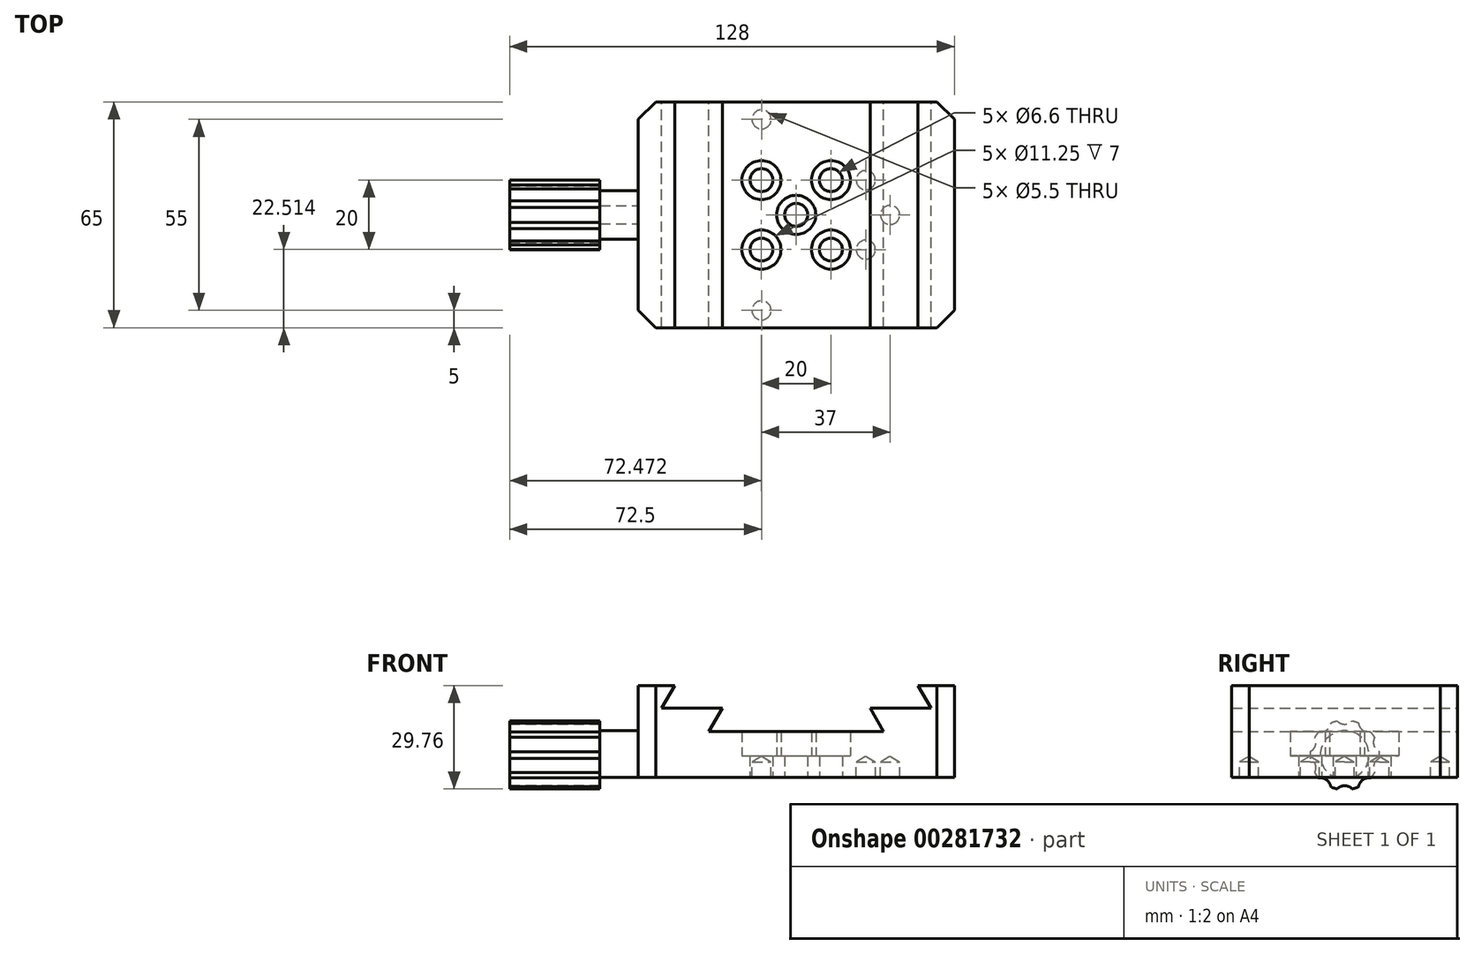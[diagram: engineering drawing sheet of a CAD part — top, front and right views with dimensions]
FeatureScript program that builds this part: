
annotation { "Feature Type Name" : "Feature", "Feature Type Description" : "" }
export const myFeature = defineFeature(function(context is Context, id is Id, definition is map)
    precondition{}
    {
        {
            var Q0;
            Q0=qCreatedBy(makeId("Front.planeOp"),FACE);
            var sketch = newSketch(context, id + "F0", { "sketchPlane" : qUnion([Q0])});
            skLineSegment(sketch, "E0.bottom", {"start": v(45.5, 13.25) * mm, "end": v(35, 13.25) * mm});
            skLineSegment(sketch, "E0.top", {"start": v(45.5, -13.25) * mm, "end": v(-45.5, -13.25) * mm});
            skLineSegment(sketch, "E0.left", {"start": v(45.5, 13.25) * mm, "end": v(45.5, -13.25) * mm});
            skLineSegment(sketch, "E0.right", {"start": v(-45.5, 13.25) * mm, "end": v(-45.5, -13.25) * mm});
            skPoint(sketch, "E0.middle", {"position": v(0, 0) * mm});
            skLineSegment(sketch, "E1", {"start": v(-35, 13.25) * mm, "end": v(-38.75, 6.75) * mm});
            skLineSegment(sketch, "E2", {"start": v(-38.75, 6.75) * mm, "end": v(-21.25, 6.75) * mm});
            skLineSegment(sketch, "E3", {"start": v(-25.15, 0) * mm, "end": v(0, 0) * mm});
            skLineSegment(sketch, "E4", {"start": v(-25.15, 0) * mm, "end": v(-21.25, 6.75) * mm});
            skLineSegment(sketch, "E5.MirrorCS", {"start": v(25.15, 0) * mm, "end": v(0, 0) * mm});
            skLineSegment(sketch, "E6.MirrorCS", {"start": v(25.15, 0) * mm, "end": v(21.25, 6.75) * mm});
            skLineSegment(sketch, "E7.MirrorCS", {"start": v(35, 13.25) * mm, "end": v(38.75, 6.75) * mm});
            skLineSegment(sketch, "E8.MirrorCS", {"start": v(38.75, 6.75) * mm, "end": v(21.25, 6.75) * mm});
            skLineSegment(sketch, "E9.trimOffspring", {"start": v(-35, 13.25) * mm, "end": v(-45.5, 13.25) * mm});
            skSolve(sketch);
        }
        {
            var Q0;
            Q0 = qSketchRegion(id + "F0", true);
            extrude(context, id + "F1", {"entities" : qUnion([Q0]), "depth" : 65 * mm, "offsetDistance" : 25 * mm});
        }
        {
            var Q0;
            Q0=makeQuery(id+"F1.opExtrude","CAP_EDGE",EDGE,{"disambiguationData":[OSD([sQuery(id+"F0.wireOp",EDGE,"E0.left")])],"isStart":false});
            var Q1;
            Q1=makeQuery(id+"F1.opExtrude","CAP_EDGE",EDGE,{"disambiguationData":[OSD([sQuery(id+"F0.wireOp",EDGE,"E0.left")])],"isStart":true});
            var Q2;
            Q2=makeQuery(id+"F1.opExtrude","CAP_EDGE",EDGE,{"disambiguationData":[OSD([sQuery(id+"F0.wireOp",EDGE,"E0.right")])],"isStart":false});
            var Q3;
            Q3=makeQuery(id+"F1.opExtrude","CAP_EDGE",EDGE,{"disambiguationData":[OSD([sQuery(id+"F0.wireOp",EDGE,"E0.right")])],"isStart":true});
            chamfer(context, id + "F2", {"entities" : qUnion([Q0, Q1, Q2, Q3]), "width" : 5 * mm, "tangentPropagation" : true});
        }
        {
            var Q0;
            Q0=makeQuery(id+"F1.opExtrude","SWEPT_FACE",FACE,{"disambiguationData":[OSD([sQuery(id+"F0.wireOp",EDGE,"E0.top")])]});
            var sketch = newSketch(context, id + "F3", { "sketchPlane" : qUnion([Q0])});
            skLineSegment(sketch, "E10", {"start": v(-58.08, 32.5) * mm, "end": v(66.9, 32.5) * mm, "construction": true});
            skLineSegment(sketch, "E11", {"start": v(0, 65) * mm, "end": v(0, 32.5) * mm, "construction": true});
            skLineSegment(sketch, "E12", {"start": v(0, 32.5) * mm, "end": v(0, 0) * mm, "construction": true});
            skLineSegment(sketch, "E13", {"start": v(-52.73, 42.5) * mm, "end": v(64.58, 42.5) * mm, "construction": true});
            skLineSegment(sketch, "E14", {"start": v(-52.06, 22.5) * mm, "end": v(64.58, 22.5) * mm, "construction": true});
            skLineSegment(sketch, "E15", {"start": v(10, 71.2) * mm, "end": v(10, -10.8) * mm, "construction": true});
            skLineSegment(sketch, "E16", {"start": v(-10, 70.97) * mm, "end": v(-10, -12.66) * mm, "construction": true});
            skCircle(sketch, "E17", {"center": v(-10, 42.5) * mm, "radius": 3.25 * mm});
            skCircle(sketch, "E18", {"center": v(10, 42.5) * mm, "radius": 3.25 * mm});
            skCircle(sketch, "E19", {"center": v(10, 22.5) * mm, "radius": 3.25 * mm});
            skCircle(sketch, "E20", {"center": v(-10, 22.5) * mm, "radius": 3.25 * mm});
            skCircle(sketch, "E21", {"center": v(0, 32.5) * mm, "radius": 3.25 * mm});
            skLineSegment(sketch, "E22", {"start": v(20, -6.44) * mm, "end": v(20, 70.45) * mm, "construction": true});
            skLineSegment(sketch, "E23", {"start": v(27, -7.6) * mm, "end": v(27, 72.31) * mm, "construction": true});
            skCircle(sketch, "E24", {"center": v(27, 32.5) * mm, "radius": 4.57 * mm});
            skCircle(sketch, "E25", {"center": v(20, 22.5) * mm, "radius": 3.73 * mm});
            skCircle(sketch, "E26", {"center": v(20, 42.5) * mm, "radius": 4.4 * mm});
            skLineSegment(sketch, "E27", {"start": v(35.3, 5) * mm, "end": v(-26.02, 5) * mm, "construction": true});
            skLineSegment(sketch, "E28", {"start": v(33.92, 60) * mm, "end": v(-26.02, 60) * mm, "construction": true});
            skCircle(sketch, "E29", {"center": v(-10, 5) * mm, "radius": 6.46 * mm});
            skCircle(sketch, "E30", {"center": v(-10, 60) * mm, "radius": 6.14 * mm});
            skSolve(sketch);
        }
        {
            var Q0;
            Q0=makeQuery(id+"F1.opExtrude","SWEPT_FACE",FACE,{"disambiguationData":[OSD([sQuery(id+"F0.wireOp",EDGE,"E3"),sQuery(id+"F0.wireOp",EDGE,"E5.MirrorCS")])]});
            var sketch = newSketch(context, id + "F4", { "sketchPlane" : qUnion([Q0])});
            skLineSegment(sketch, "E31", {"start": v(-58.1, -32.49) * mm, "end": v(66.88, -32.49) * mm, "construction": true});
            skLineSegment(sketch, "E32", {"start": v(-0.03, 0.01) * mm, "end": v(-0.03, -32.49) * mm, "construction": true});
            skLineSegment(sketch, "E33", {"start": v(-0.03, -32.49) * mm, "end": v(-0.03, -64.99) * mm, "construction": true});
            skLineSegment(sketch, "E34", {"start": v(-52.76, -22.49) * mm, "end": v(64.55, -22.49) * mm, "construction": true});
            skLineSegment(sketch, "E35", {"start": v(-52.1, -42.49) * mm, "end": v(64.55, -42.49) * mm, "construction": true});
            skLineSegment(sketch, "E36", {"start": v(9.97, 6.21) * mm, "end": v(9.97, -75.79) * mm, "construction": true});
            skLineSegment(sketch, "E37", {"start": v(-10.03, 5.98) * mm, "end": v(-10.03, -77.65) * mm, "construction": true});
            skCircle(sketch, "E38", {"center": v(-10.03, -22.49) * mm, "radius": 3.25 * mm});
            skCircle(sketch, "E39", {"center": v(9.97, -22.49) * mm, "radius": 3.25 * mm});
            skCircle(sketch, "E40", {"center": v(9.97, -42.49) * mm, "radius": 3.25 * mm});
            skCircle(sketch, "E41", {"center": v(-10.03, -42.49) * mm, "radius": 3.25 * mm});
            skCircle(sketch, "E42", {"center": v(-0.03, -32.49) * mm, "radius": 3.25 * mm});
            skSolve(sketch);
        }
        {
            var Q0;
            Q0=sQuery(id+"F4.wireOp",VERTEX,"E39.center");
            var Q1;
            Q1=sQuery(id+"F4.wireOp",VERTEX,"E38.center");
            var Q2;
            Q2=sQuery(id+"F4.wireOp",VERTEX,"E41.center");
            var Q3;
            Q3=sQuery(id+"F4.wireOp",VERTEX,"E40.center");
            var Q4;
            Q4=sQuery(id+"F4.wireOp",VERTEX,"E42.center");
            var Q5;
            Q5=makeQuery(id+"F1.opExtrude","SWEPT_BODY",BODY,{"disambiguationData":[OSD([sQuery(id+"F0.wireOp",EDGE,"E0.bottom"),sQuery(id+"F0.wireOp",EDGE,"E0.top"),sQuery(id+"F0.wireOp",EDGE,"E0.left"),sQuery(id+"F0.wireOp",EDGE,"E0.right"),sQuery(id+"F0.wireOp",EDGE,"E1"),sQuery(id+"F0.wireOp",EDGE,"E2"),sQuery(id+"F0.wireOp",EDGE,"E3"),sQuery(id+"F0.wireOp",EDGE,"E4"),sQuery(id+"F0.wireOp",EDGE,"E5.MirrorCS"),sQuery(id+"F0.wireOp",EDGE,"E6.MirrorCS"),sQuery(id+"F0.wireOp",EDGE,"E7.MirrorCS"),sQuery(id+"F0.wireOp",EDGE,"E8.MirrorCS"),sQuery(id+"F0.wireOp",EDGE,"E9.trimOffspring")])]});
            hole(context, id + "F5", {"style" : HoleStyle.C_BORE, "endStyle" : HoleEndStyle.THROUGH, "holeDiameter" : 6.6 * mm, "cBoreDiameter" : 11.25 * mm, "cBoreDepth" : 7 * mm, "majorDiameter" : 5 * mm, "isTappedThrough" : true, "tappedDepth" : 12 * mm, "tapClearance" : 3, "locations" : qUnion([Q0, Q1, Q2, Q3, Q4]), "scope" : qUnion([Q5]), "startStyle" : HoleStartStyle.SKETCH});
        }
        {
            var Q0;
            Q0=sQuery(id+"F3.wireOp",VERTEX,"E24.center");
            var Q1;
            Q1=sQuery(id+"F3.wireOp",VERTEX,"E25.center");
            var Q2;
            Q2=sQuery(id+"F3.wireOp",VERTEX,"E26.center");
            var Q3;
            Q3=sQuery(id+"F3.wireOp",VERTEX,"E29.center");
            var Q4;
            Q4=sQuery(id+"F3.wireOp",VERTEX,"E30.center");
            var Q5;
            Q5=makeQuery(id+"F1.opExtrude","SWEPT_BODY",BODY,{"disambiguationData":[OSD([sQuery(id+"F0.wireOp",EDGE,"E0.bottom"),sQuery(id+"F0.wireOp",EDGE,"E0.top"),sQuery(id+"F0.wireOp",EDGE,"E0.left"),sQuery(id+"F0.wireOp",EDGE,"E0.right"),sQuery(id+"F0.wireOp",EDGE,"E1"),sQuery(id+"F0.wireOp",EDGE,"E2"),sQuery(id+"F0.wireOp",EDGE,"E3"),sQuery(id+"F0.wireOp",EDGE,"E4"),sQuery(id+"F0.wireOp",EDGE,"E5.MirrorCS"),sQuery(id+"F0.wireOp",EDGE,"E6.MirrorCS"),sQuery(id+"F0.wireOp",EDGE,"E7.MirrorCS"),sQuery(id+"F0.wireOp",EDGE,"E8.MirrorCS"),sQuery(id+"F0.wireOp",EDGE,"E9.trimOffspring")])]});
            hole(context, id + "F6", {"style" : HoleStyle.SIMPLE, "endStyle" : HoleEndStyle.BLIND, "standardTappedOrClearance" : lookupTablePath({ "standard" : "ISO", "fit" : "Normal", "size" : "M5", "type" : "Clearance" }), "standardBlindInLast" : lookupTablePath({ "fit" : "Standard", "standard" : "ISO", "size" : "M5", "type" : "Clearance" }), "holeDiameter" : 5.5 * mm, "majorDiameter" : 5 * mm, "holeDepth" : 4.5 * mm, "isTappedThrough" : true, "tappedDepth" : 12 * mm, "tapClearance" : 3, "locations" : qUnion([Q0, Q1, Q2, Q3, Q4]), "scope" : qUnion([Q5]), "startStyle" : HoleStartStyle.SKETCH});
        }
        {
            var Q0;
            Q0=makeQuery(id+"F1.opExtrude","SWEPT_FACE",FACE,{"disambiguationData":[OSD([sQuery(id+"F0.wireOp",EDGE,"E0.right")])]});
            var sketch = newSketch(context, id + "F7", { "sketchPlane" : qUnion([Q0])});
            skLineSegment(sketch, "E43", {"start": v(32.5, -6.75) * mm, "end": v(60, -6.75) * mm, "construction": true});
            skLineSegment(sketch, "E44", {"start": v(32.5, 11.33) * mm, "end": v(32.5, -24.83) * mm, "construction": true});
            skLineSegment(sketch, "E45", {"start": v(32.5, -6.75) * mm, "end": v(5, -6.75) * mm, "construction": true});
            skCircle(sketch, "E46", {"center": v(32.5, -6.75) * mm, "radius": 7 * mm});
            skSolve(sketch);
        }
        {
            var Q0;
            {var subQ0=sQuery(id+"F7.wireOp",EDGE,"E46");var subQ1=makeQuery(id+"F1.opExtrude","SWEPT_EDGE",EDGE,{"disambiguationData":[OSD([sQuery(id+"F0.wireOp",EDGE,"E0.top"),sQuery(id+"F0.wireOp",EDGE,"E0.right")])]});var subQ2=makeQuery(id+"F7.imprint","INTERSECT",VERTEX,{"disambiguationData":[OD(0.0)],"derivedFrom":[subQ1,subQ0]});Q0=makeQuery(id+"F7.imprint","IMPRINT",FACE,{"disambiguationData":[TD([[makeQuery(id+"F7.imprint","IMPRINT",EDGE,{"disambiguationData":[TD([[subQ2,1.0]])],"derivedFrom":subQ0}),1.0]])]});}
            extrude(context, id + "F8", {"entities" : qUnion([Q0]), "depth" : 37 * mm, "offsetDistance" : 25 * mm});
        }
        {
            var Q0;
            Q0=makeQuery(id+"F8.opExtrude","CAP_FACE",FACE,{"disambiguationData":[OSD([sQuery(id+"F0.wireOp",EDGE,"E0.top"),sQuery(id+"F0.wireOp",EDGE,"E0.right"),sQuery(id+"F7.wireOp",EDGE,"E46")])],"isStart":false});
            var sketch = newSketch(context, id + "F9", { "sketchPlane" : qUnion([Q0])});
            skCircle(sketch, "E47", {"center": v(32.5, -6.75) * mm, "radius": 10 * mm});
            skLineSegment(sketch, "E48", {"start": v(32.5, -6.75) * mm, "end": v(32.5, 12.15) * mm, "construction": true});
            skCircle(sketch, "E49", {"center": v(32.5, 5.1) * mm, "radius": 3 * mm});
            skLineSegment(sketch, "E50", {"start": v(32.5, -6.75) * mm, "end": v(42.62, 7.18) * mm, "construction": true});
            skCircle(sketch, "E51.1.0", {"center": v(25.54, 2.84) * mm, "radius": 3 * mm});
            skCircle(sketch, "E51.2.0", {"center": v(21.23, -3.09) * mm, "radius": 3 * mm});
            skCircle(sketch, "E51.3.0", {"center": v(21.23, -10.41) * mm, "radius": 3 * mm});
            skCircle(sketch, "E51.4.0", {"center": v(25.54, -16.34) * mm, "radius": 3 * mm});
            skCircle(sketch, "E51.5.0", {"center": v(32.5, -18.6) * mm, "radius": 3 * mm});
            skCircle(sketch, "E51.6.0", {"center": v(39.46, -16.34) * mm, "radius": 3 * mm});
            skCircle(sketch, "E51.7.0", {"center": v(43.77, -10.41) * mm, "radius": 3 * mm});
            skCircle(sketch, "E51.8.0", {"center": v(43.77, -3.09) * mm, "radius": 3 * mm});
            skCircle(sketch, "E51.9.0", {"center": v(39.46, 2.84) * mm, "radius": 3 * mm});
            skSolve(sketch);
        }
        {
            var Q0;
            Q0=makeQuery(id+"F9.imprint","IMPRINT",FACE,{"disambiguationData":[TD([[makeQuery(id+"F9.imprint","IMPRINT",EDGE,{"derivedFrom":makeQuery(id+"F8.opExtrude","CAP_EDGE",EDGE,{"disambiguationData":[OSD([sQuery(id+"F7.wireOp",EDGE,"E46")])],"isStart":false})}),-1.0]])]});
            var Q1;
            Q1=makeQuery(id+"F9.imprint","IMPRINT",FACE,{"disambiguationData":[TD([[makeQuery(id+"F9.imprint","IMPRINT",EDGE,{"derivedFrom":makeQuery(id+"F8.opExtrude","CAP_EDGE",EDGE,{"disambiguationData":[OSD([sQuery(id+"F7.wireOp",EDGE,"E46")])],"isStart":false})}),1.0]])]});
            extrude(context, id + "F10", {"entities" : qUnion([Q0, Q1]), "operationType" : NewBodyOperationType.ADD, "oppositeDirection" : true, "depth" : 26 * mm, "offsetDistance" : 25 * mm});
        }
    });
